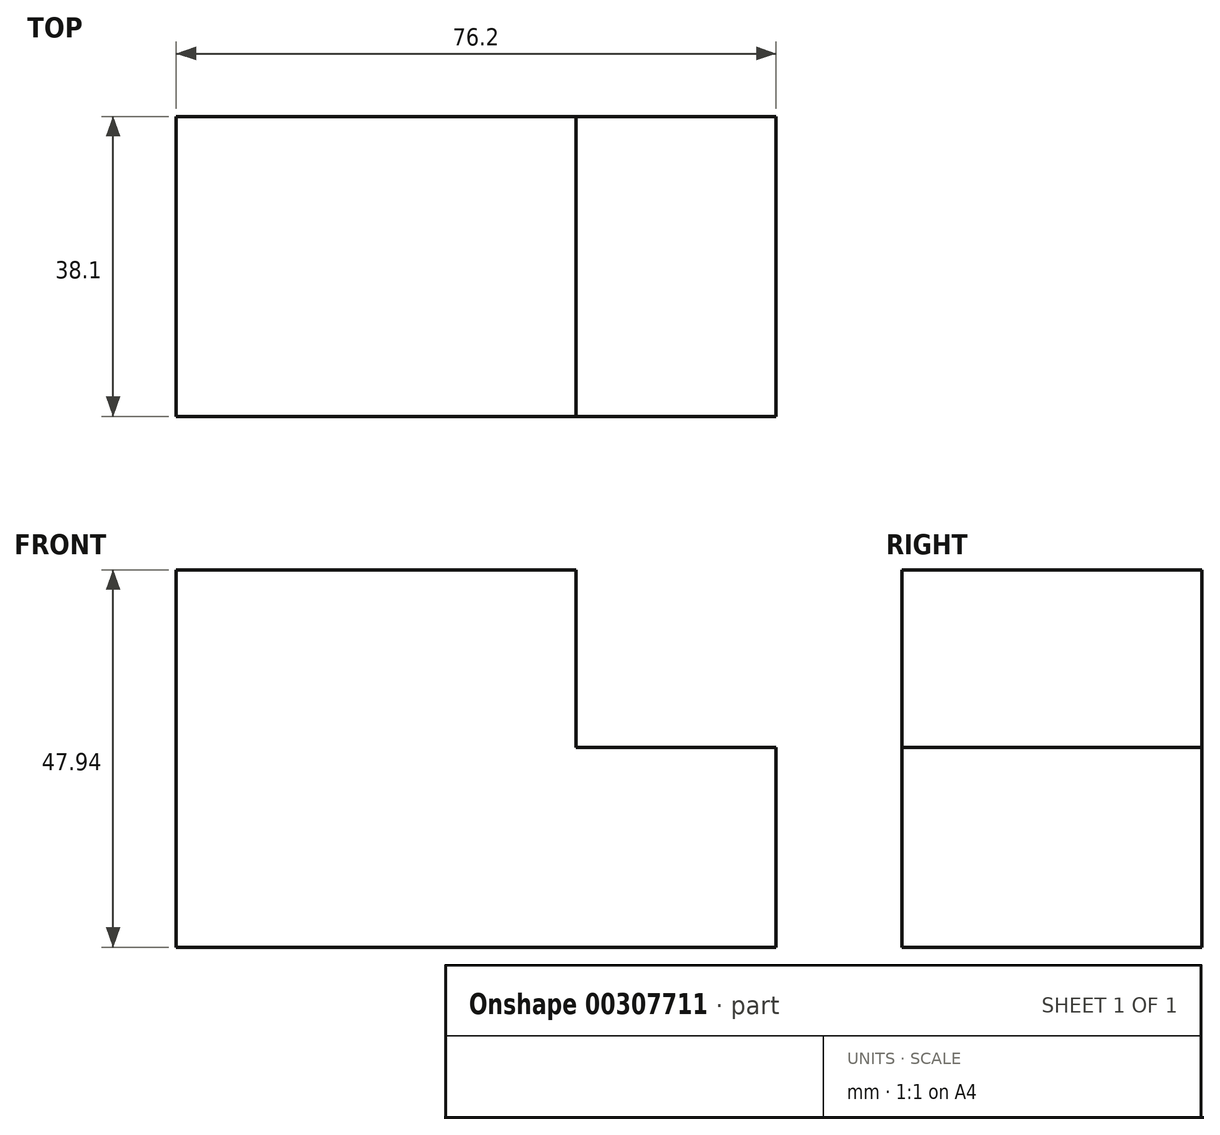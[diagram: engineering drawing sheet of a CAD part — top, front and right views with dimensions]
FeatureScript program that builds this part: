
annotation { "Feature Type Name" : "Feature", "Feature Type Description" : "" }
export const myFeature = defineFeature(function(context is Context, id is Id, definition is map)
    precondition{}
    {
        {
            var Q0;
            Q0=qCreatedBy(makeId("Front.planeOp"),FACE);
            var sketch = newSketch(context, id + "F0", { "sketchPlane" : qUnion([Q0])});
            skLineSegment(sketch, "E0", {"start": v(-25.13, -42.43) * mm, "end": v(51.07, -42.43) * mm});
            skLineSegment(sketch, "E1", {"start": v(51.07, -42.43) * mm, "end": v(51.07, -17.03) * mm});
            skLineSegment(sketch, "E2", {"start": v(51.07, -17.03) * mm, "end": v(25.67, -17.03) * mm});
            skLineSegment(sketch, "E3", {"start": v(25.67, -17.03) * mm, "end": v(25.67, 5.51) * mm});
            skLineSegment(sketch, "E4", {"start": v(25.67, 5.51) * mm, "end": v(-25.13, 5.51) * mm});
            skLineSegment(sketch, "E5", {"start": v(-25.13, 5.51) * mm, "end": v(-25.13, -42.43) * mm});
            skSolve(sketch);
        }
        {
            var Q0;
            Q0=makeQuery(id+"F0.imprint","IMPRINT",FACE,{"disambiguationData":[TD([[makeQuery(id+"F0.imprint","IMPRINT",EDGE,{"derivedFrom":sQuery(id+"F0.wireOp",EDGE,"E0")}),1.0]])]});
            extrude(context, id + "F1", {"entities" : qUnion([Q0]), "depth" : 38.1 * mm});
        }
    });
